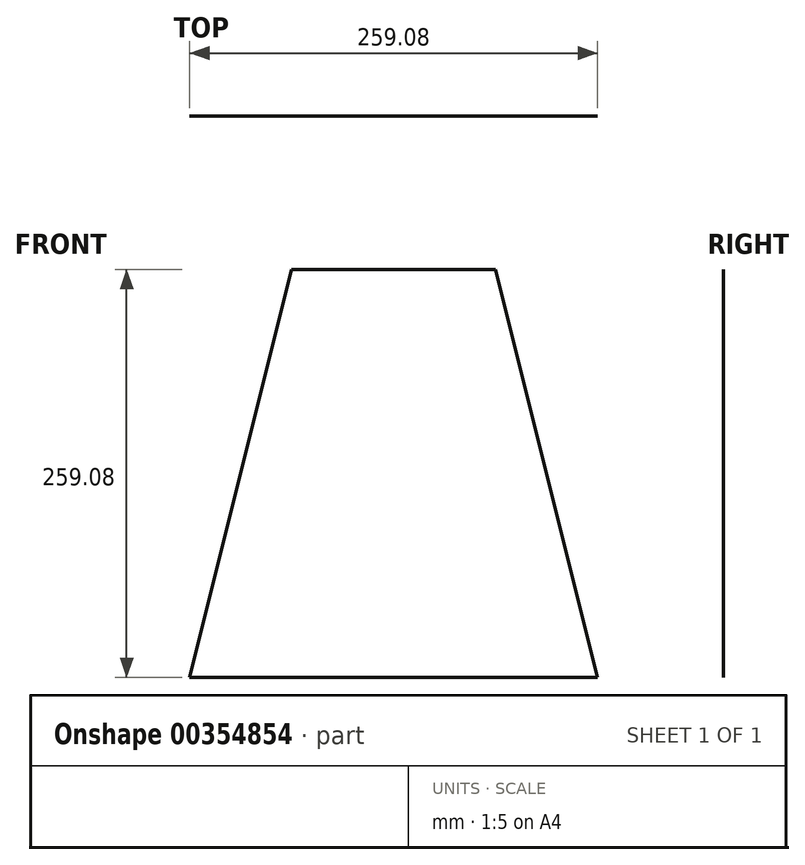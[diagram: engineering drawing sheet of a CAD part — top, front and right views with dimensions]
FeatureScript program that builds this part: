
annotation { "Feature Type Name" : "Feature", "Feature Type Description" : "" }
export const myFeature = defineFeature(function(context is Context, id is Id, definition is map)
    precondition{}
    {
        {
            var Q0;
            Q0=qCreatedBy(makeId("Front.planeOp"),FACE);
            var sketch = newSketch(context, id + "F0", { "sketchPlane" : qUnion([Q0])});
            skLineSegment(sketch, "E0", {"start": v(-162.7, 0) * mm, "end": v(162.3, 0) * mm, "construction": true});
            skLineSegment(sketch, "E1", {"start": v(0, 417.2) * mm, "end": v(0, -113.48) * mm, "construction": true});
            skLineSegment(sketch, "E2", {"start": v(-129.54, 0) * mm, "end": v(129.54, 0) * mm});
            skLineSegment(sketch, "E3", {"start": v(0, 0) * mm, "end": v(0, 259.08) * mm});
            skLineSegment(sketch, "E4", {"start": v(-64.77, 259.08) * mm, "end": v(64.77, 259.08) * mm});
            skLineSegment(sketch, "E5", {"start": v(-64.77, 259.08) * mm, "end": v(-129.54, 0) * mm});
            skLineSegment(sketch, "E6", {"start": v(64.77, 259.08) * mm, "end": v(129.54, 0) * mm});
            skSolve(sketch);
        }
        {
            var Q0;
            Q0 = qSketchRegion(id + "F0", true);
            extrude(context, id + "F1", {"entities" : qUnion([Q0]), "endBound" : BoundingType.SYMMETRIC, "depth" : 1 / 203.2 * mm});
        }
    });
